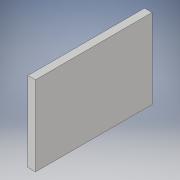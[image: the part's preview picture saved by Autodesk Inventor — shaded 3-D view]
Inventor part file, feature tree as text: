
AUTODESK INVENTOR PART (.ipt)
format: ipt  version: 2019 (Build 230136000, 136)  size: 87,552 bytes
history: native  units: in
note: dims shown in document units (in); Inventor stores cm internally (conversion verified against a paired STEP export)
features: extrude x1, sketch x1
ambient origin geometry x8: Origin, YZ Plane, XZ Plane, XY Plane, X Axis, Y Axis, Z Axis, Center Point
bodies: Solid1 (feature_tree)
feature tree (2):
  extrude  "Extrusion1"  Depth=4.852in
  sketch  "Sketch1"  dims[d0=3.315in d1=4.852in d2=0.315in d3=0.0in]
